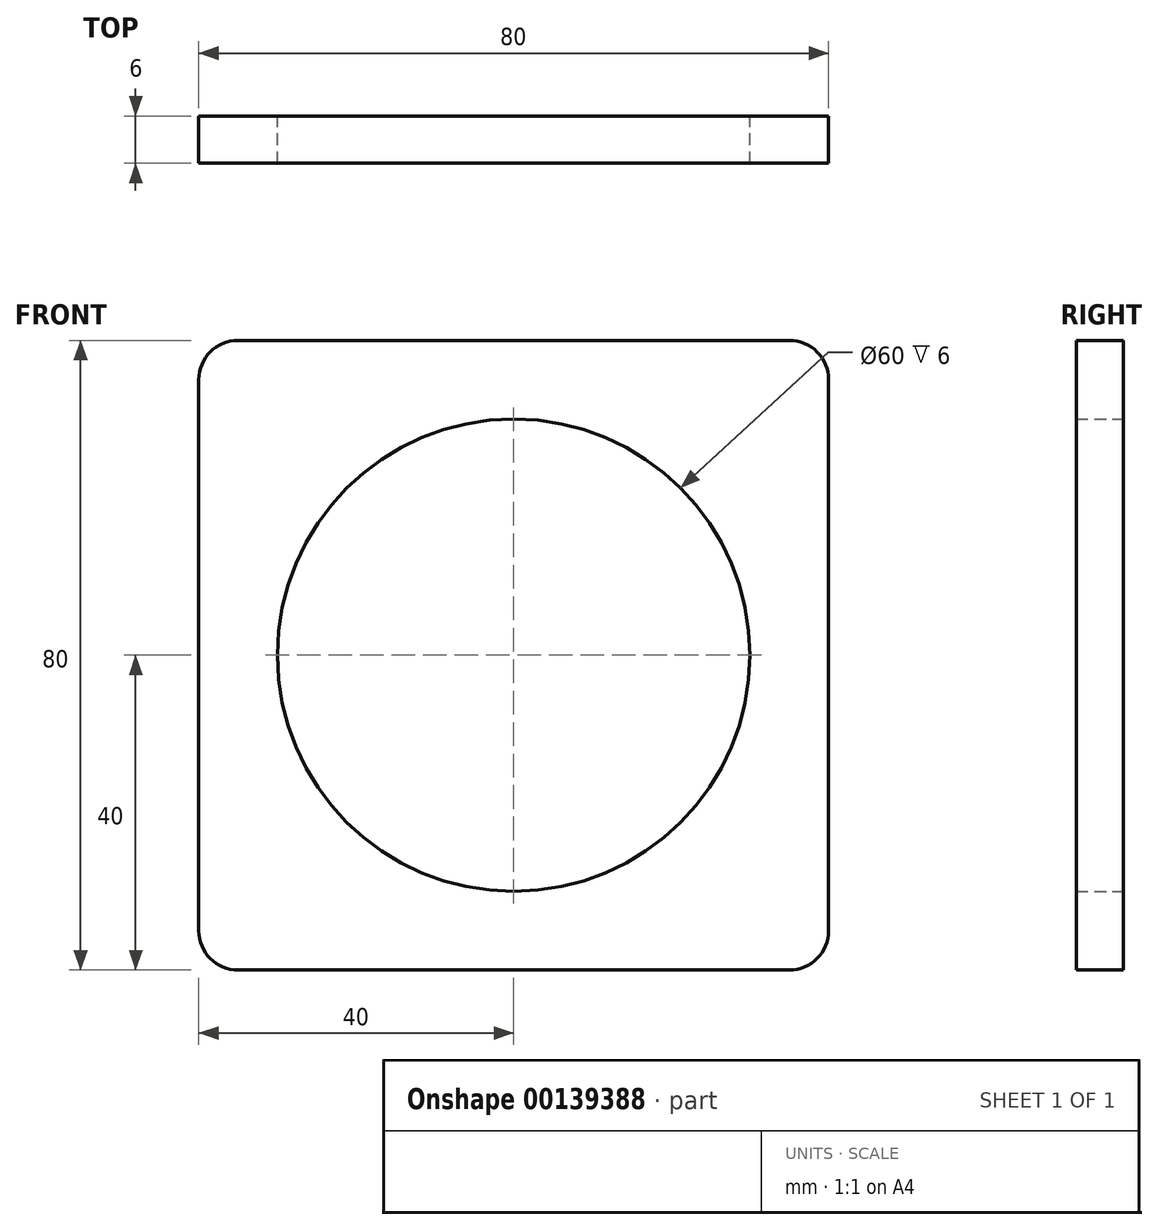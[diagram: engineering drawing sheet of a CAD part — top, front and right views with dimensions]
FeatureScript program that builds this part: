
annotation { "Feature Type Name" : "Feature", "Feature Type Description" : "" }
export const myFeature = defineFeature(function(context is Context, id is Id, definition is map)
    precondition{}
    {
        {
            var Q0;
            Q0=qCreatedBy(makeId("Front.planeOp"),FACE);
            var sketch = newSketch(context, id + "F0", { "sketchPlane" : qUnion([Q0])});
            skLineSegment(sketch, "E0.bottom", {"start": v(-5, 0) * mm, "end": v(-75, 0) * mm});
            skLineSegment(sketch, "E0.top", {"start": v(-5, 80) * mm, "end": v(-75, 80) * mm});
            skLineSegment(sketch, "E0.left", {"start": v(0, 5) * mm, "end": v(0, 75) * mm});
            skLineSegment(sketch, "E0.right", {"start": v(-80, 5) * mm, "end": v(-80, 75) * mm});
            skPoint(sketch, "E1.visualSharp", {"position": v(-80, 80) * mm});
            skArc(sketch, "E1.filletArc", {"start": v(-75, 80) * mm, "mid": v(-78.54, 78.54) * mm, "end": v(-80, 75) * mm});
            skPoint(sketch, "E2.visualSharp", {"position": v(0, 80) * mm});
            skArc(sketch, "E2.filletArc", {"start": v(0, 75) * mm, "mid": v(-1.46, 78.54) * mm, "end": v(-5, 80) * mm});
            skPoint(sketch, "E3.visualSharp", {"position": v(-80, 0) * mm});
            skArc(sketch, "E3.filletArc", {"start": v(-80, 5) * mm, "mid": v(-78.54, 1.46) * mm, "end": v(-75, 0) * mm});
            skPoint(sketch, "E4.visualSharp", {"position": v(0, 0) * mm});
            skArc(sketch, "E4.filletArc", {"start": v(-5, 0) * mm, "mid": v(-1.46, 1.46) * mm, "end": v(0, 5) * mm});
            skPoint(sketch, "E5.visualSharp", {"position": v(-65, 5) * mm});
            skCircle(sketch, "E6", {"center": v(-40, 40) * mm, "radius": 30 * mm});
            skSolve(sketch);
        }
        {
            var Q0;
            Q0=makeQuery(id+"F0.imprint","IMPRINT",FACE,{"disambiguationData":[TD([[makeQuery(id+"F0.imprint","IMPRINT",EDGE,{"derivedFrom":sQuery(id+"F0.wireOp",EDGE,"E0.bottom")}),-1.0]])]});
            extrude(context, id + "F1", {"entities" : qUnion([Q0]), "depth" : 6 * mm});
        }
    });
